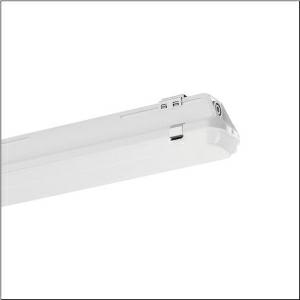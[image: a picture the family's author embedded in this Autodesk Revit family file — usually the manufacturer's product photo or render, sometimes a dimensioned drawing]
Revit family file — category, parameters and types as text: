
# Revit family: monsun_21_51fb10dp660b
name_source: partatom
category: Lighting Fixtures
units: mm (PartAtom-declared; Revit-internal decimal feet)

## family parameters
Cut with Voids When Loaded = No
Host = Face
Light Source = No
Part Type = Normal
Room Calculation Point = No
Round Connector Dimension = Use Diameter
Shared = No

## types (1)
- --- (1 x LED, 6060 lm, 39.4 W, 6500K)
    Apparent Load = 39 VA
    CIE Flux Codes = 47 77 93 94 100
    Color Rendering = 80
    Color Temperature = 6500K
    Default Elevation = 1800 mm
    Description = Monsun 21, damp-proof luminaire, chain hanger, primary optical cover: enclosure, of PMMA, light emission: direct distribution, primary light characteristic: symmetric, installation type: suspended mounting, surface-mounted, horizontal mounting, vertical mounting, LED, rated luminous flux: 6.060lm, luminous efficacy: 154lm/W, light colour: 865, colour temperature: 6500K, control gear: DALI 2, with terminal, 5-pole, max. 2.5mm², mains connection: 220..240V, AC, 50/60Hz, rated input power: 39W, housing, of glass-fibre reinforced polyester, uncoated, bright grey, incl. chain hanger, length: 1.590mm, width: 90mm, height: 88mm, clip for enclosure, of stainless steel (V2A), ceiling mounting element, of stainless steel (V2A), chain hanger, of stainless steel (V2A), protection rating (complete): IP66, insulation class (complete): insulation class I (protective earthing), certification: CE, ENEC, VDE, UKCA, protection symbol: D, impact resistance: IK04, permissible operating ambient temperature: -25..+35°C, standard: EN 50419, EN 60598-2-1, corresponds to IFS (International Featured Standards) requirements for safety and quality in the food industry, for indoor or canopied outdoor use, no direct snow, no direct sun, no direct rain, contact your sales advisor before using the luminaires in applications with unclear chemical exposure, large temperature fluctuations or condensation-forming humidity, LABS conformity tested according to VDMA 24364:2018-05, packaging unit: 1 piece
    Height = 89 mm
    Lamp = 1 x LED
    Lamp Light Flux = 6060 lm
    Lamp Power = 39.4 W
    Lamp count = 1
    Length = 1590 mm
    Luminous efficacy = 154 lm/W
    Manufacturer = Siteco
    ModVariant = No
    Model = 51FB10DP660B
    Mounting Place = Ceiling
    Mounting Type = Surface mounted
    Number of Poles = 1
    OnlyDefault = Yes
    Power Factor = 1
    Product Name = Monsun 21
    Product group = damp-proof luminaire
    ProductGroupID = 300
    Protection Class = Protection class I
    Protection Degree = IP 66
    RLX_Detail_Level = 1
    RLX_Emergency_Light_Flux = 0 lm
    RLX_Emergency_Type = 0
    RLX_Emergency_Type_DB = No
    RlxData = <blob elided: 92209 chars, md5=734d6383>
    Socket = socket
    Standby Power = 0 W
    System Light Flux = 6060 lm
    System Power = 39 W
    Type Comments = factory setting: luminous flux: 100 % | dim-lin: 254 | 261 mA
    Type Image = l_1319656.jpg
    URL = http://relux.com
    VarID = @adj_194775
    Voltage = 0 V
    Weight = 0.00 kg
    Width = 90 mm

## geometry (parser evidence)
native form markers: Blend x4, Sweep x13
no freeform markers — native parametric forms only
